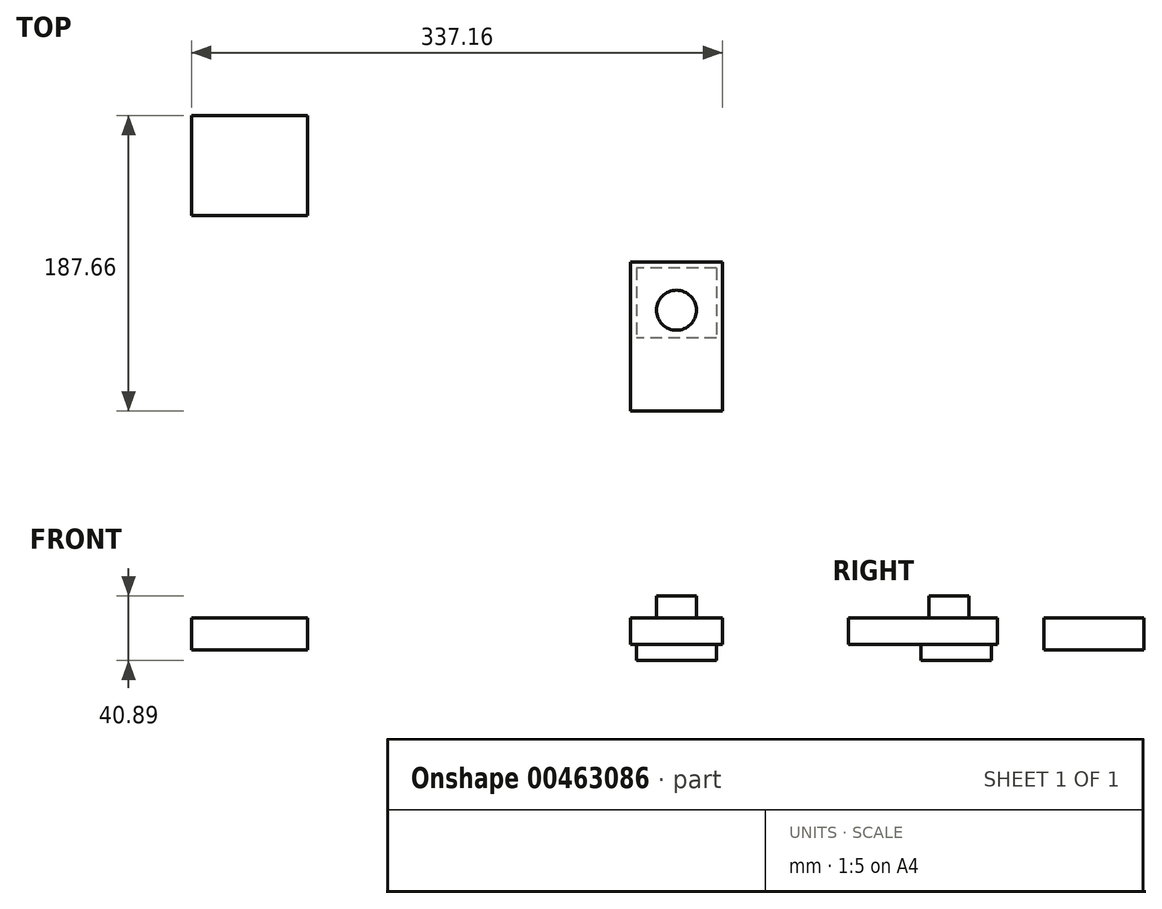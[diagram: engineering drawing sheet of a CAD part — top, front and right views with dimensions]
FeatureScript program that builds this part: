
annotation { "Feature Type Name" : "Feature", "Feature Type Description" : "" }
export const myFeature = defineFeature(function(context is Context, id is Id, definition is map)
    precondition{}
    {
        {
            var Q0;
            Q0=qCreatedBy(makeId("Top.planeOp"),FACE);
            var sketch = newSketch(context, id + "F0", { "sketchPlane" : qUnion([Q0])});
            skLineSegment(sketch, "E0.bottom", {"start": v(0, 0) * mm, "end": v(58.42, 0) * mm});
            skLineSegment(sketch, "E0.top", {"start": v(0, -94.49) * mm, "end": v(58.42, -94.49) * mm});
            skLineSegment(sketch, "E0.left", {"start": v(0, 0) * mm, "end": v(0, -94.49) * mm});
            skLineSegment(sketch, "E0.right", {"start": v(58.42, 0) * mm, "end": v(58.42, -94.49) * mm});
            skCircle(sketch, "E1", {"center": v(29.21, -30.48) * mm, "radius": 12.7 * mm});
            skPoint(sketch, "E1.centerSnap0", {"position": v(29.21, 0) * mm});
            skSolve(sketch);
        }
        {
            var Q0;
            Q0=makeQuery(id+"F0.imprint","IMPRINT",FACE,{"disambiguationData":[TD([[makeQuery(id+"F0.imprint","IMPRINT",EDGE,{"derivedFrom":sQuery(id+"F0.wireOp",EDGE,"E1")}),1.0]])]});
            var Q1;
            Q1=makeQuery(id+"F0.imprint","IMPRINT",FACE,{"disambiguationData":[TD([[makeQuery(id+"F0.imprint","IMPRINT",EDGE,{"derivedFrom":sQuery(id+"F0.wireOp",EDGE,"E0.bottom")}),-1.0]])]});
            extrude(context, id + "F1", {"entities" : qUnion([Q0, Q1]), "oppositeDirection" : true, "depth" : 16.76 * mm});
        }
        {
            var Q0;
            Q0=makeQuery(id+"F0.imprint","IMPRINT",FACE,{"disambiguationData":[TD([[makeQuery(id+"F0.imprint","IMPRINT",EDGE,{"derivedFrom":sQuery(id+"F0.wireOp",EDGE,"E1")}),1.0]])]});
            extrude(context, id + "F2", {"entities" : qUnion([Q0]), "operationType" : NewBodyOperationType.ADD, "depth" : 13.97 * mm});
        }
        {
            var Q0;
            Q0=makeQuery(id+"F1.opExtrude","CAP_FACE",FACE,{"disambiguationData":[OSD([sQuery(id+"F0.wireOp",EDGE,"E0.bottom"),sQuery(id+"F0.wireOp",EDGE,"E0.top"),sQuery(id+"F0.wireOp",EDGE,"E0.left"),sQuery(id+"F0.wireOp",EDGE,"E0.right")])],"isStart":false});
            var sketch = newSketch(context, id + "F3", { "sketchPlane" : qUnion([Q0])});
            skLineSegment(sketch, "E2.bottom", {"start": v(54.6, 3.81) * mm, "end": v(3.81, 3.8) * mm});
            skLineSegment(sketch, "E2.top", {"start": v(54.6, 48.26) * mm, "end": v(3.81, 48.26) * mm});
            skLineSegment(sketch, "E2.left", {"start": v(54.6, 3.81) * mm, "end": v(54.6, 48.26) * mm});
            skLineSegment(sketch, "E2.right", {"start": v(3.81, 3.8) * mm, "end": v(3.81, 48.26) * mm});
            skSolve(sketch);
        }
        {
            var Q0;
            Q0=makeQuery(id+"F3.imprint","IMPRINT",FACE,{"disambiguationData":[TD([[makeQuery(id+"F3.imprint","IMPRINT",EDGE,{"derivedFrom":sQuery(id+"F3.wireOp",EDGE,"E2.bottom")}),-1.0]])]});
            extrude(context, id + "F4", {"entities" : qUnion([Q0]), "operationType" : NewBodyOperationType.ADD, "depth" : 10.16 * mm});
        }
        {
            var Q0;
            Q0=qCreatedBy(makeId("Top.planeOp"),FACE);
            var sketch = newSketch(context, id + "F5", { "sketchPlane" : qUnion([Q0])});
            skLineSegment(sketch, "E3.bottom", {"start": v(-278.74, 93.17) * mm, "end": v(-205.08, 93.17) * mm});
            skLineSegment(sketch, "E3.top", {"start": v(-278.74, 29.67) * mm, "end": v(-205.08, 29.67) * mm});
            skLineSegment(sketch, "E3.left", {"start": v(-278.74, 93.17) * mm, "end": v(-278.74, 29.67) * mm});
            skLineSegment(sketch, "E3.right", {"start": v(-205.08, 93.17) * mm, "end": v(-205.08, 29.67) * mm});
            skSolve(sketch);
        }
        {
            var Q0;
            Q0=makeQuery(id+"F5.imprint","IMPRINT",FACE,{"disambiguationData":[TD([[makeQuery(id+"F5.imprint","IMPRINT",EDGE,{"derivedFrom":sQuery(id+"F5.wireOp",EDGE,"E3.bottom")}),-1.0]])]});
            extrude(context, id + "F6", {"entities" : qUnion([Q0]), "oppositeDirection" : true, "depth" : 20.32 * mm});
        }
    });
